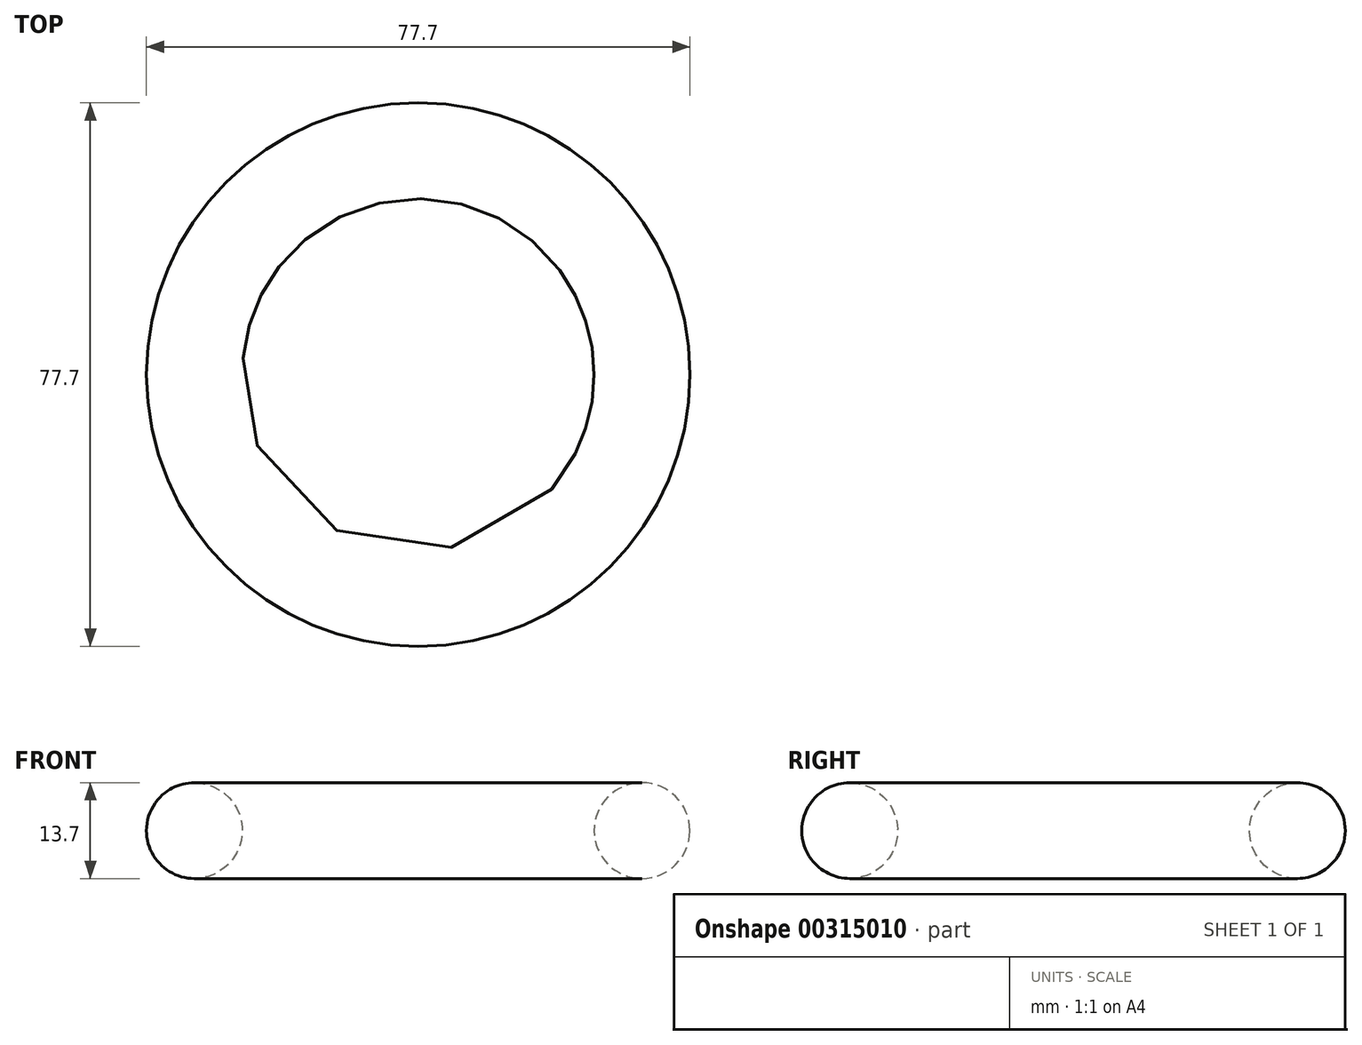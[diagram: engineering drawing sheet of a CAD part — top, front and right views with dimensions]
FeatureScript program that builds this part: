
annotation { "Feature Type Name" : "Feature", "Feature Type Description" : "" }
export const myFeature = defineFeature(function(context is Context, id is Id, definition is map)
    precondition{}
    {
        {
            var Q0;
            Q0=qCreatedBy(makeId("Front.planeOp"),FACE);
            var sketch = newSketch(context, id + "F0", { "sketchPlane" : qUnion([Q0])});
            skLineSegment(sketch, "E0", {"start": v(0, 33.2) * mm, "end": v(0, -32.8) * mm, "construction": true});
            skCircle(sketch, "E1", {"center": v(32, 0) * mm, "radius": 6.85 * mm});
            skSolve(sketch);
        }
        {
            var Q0;
            Q0=makeQuery(id+"F0.imprint","IMPRINT",FACE,{"disambiguationData":[TD([[makeQuery(id+"F0.imprint","IMPRINT",EDGE,{"derivedFrom":sQuery(id+"F0.wireOp",EDGE,"E1")}),1.0]])]});
            var Q1;
            Q1=sQuery(id+"F0.wireOp",EDGE,"E0");
            revolve(context, id + "F1", {"entities" : qUnion([Q0]), "axis" : qUnion([Q1]), "revolveType" : RevolveType.FULL});
        }
    });
